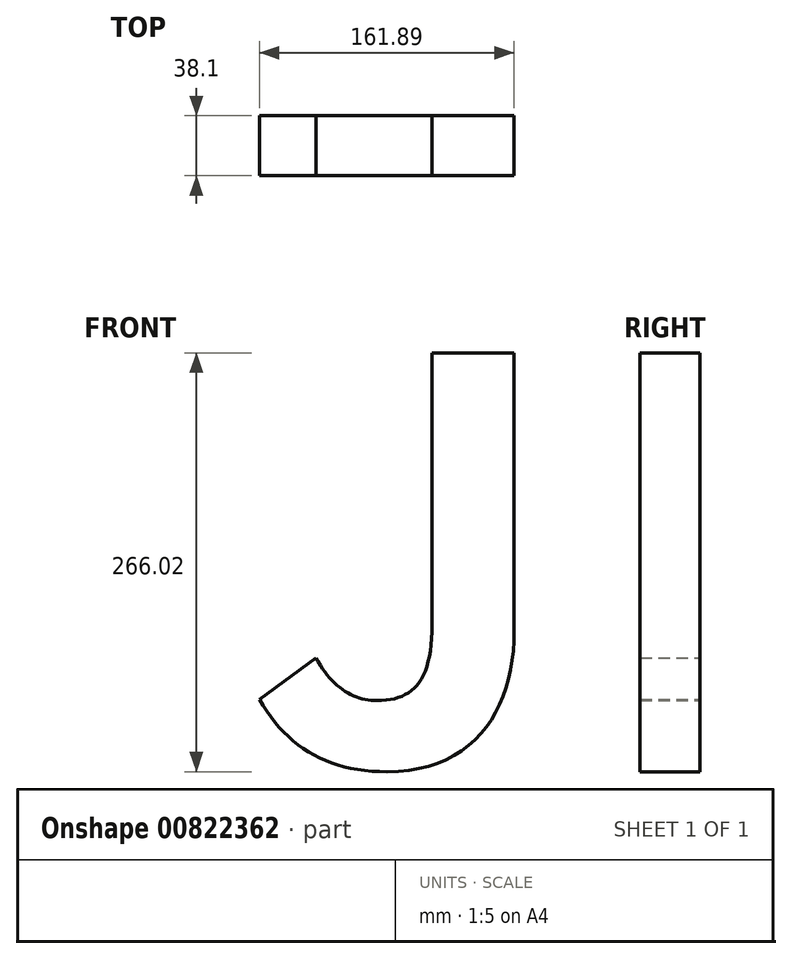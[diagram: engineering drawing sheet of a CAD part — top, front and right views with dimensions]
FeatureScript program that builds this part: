
annotation { "Feature Type Name" : "Feature", "Feature Type Description" : "" }
export const myFeature = defineFeature(function(context is Context, id is Id, definition is map)
    precondition{}
    {
        {
            var Q0;
            Q0=qCreatedBy(makeId("Front.planeOp"),FACE);
            var sketch = newSketch(context, id + "F0", { "sketchPlane" : qUnion([Q0])});
            skText(sketch, "E0", { "text": "J", "fontName": "NotoSansCJKkr-Bold.otf"});
            const initialGuessF0  = {"E0": [-0.09711, -0.127, 1, 0, 0.254]};
            skSetInitialGuess(sketch, initialGuessF0);
            skSolve(sketch);
        }
        {
            var Q0;
            Q0 = qSketchRegion(id + "F0", true);
            extrude(context, id + "F1", {"entities" : qUnion([Q0]), "depth" : 38.1 * mm, "offsetDistance" : 25.4 * mm});
        }
    });
